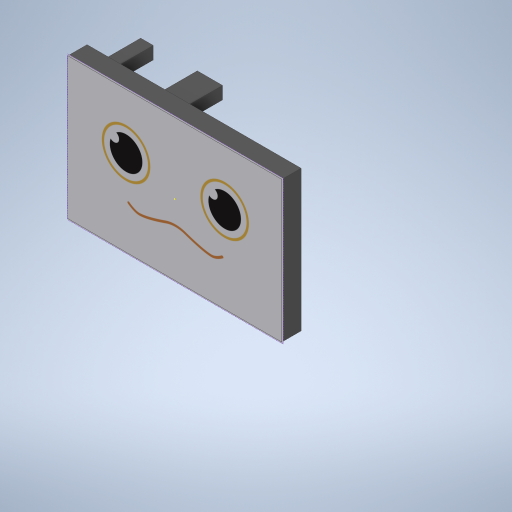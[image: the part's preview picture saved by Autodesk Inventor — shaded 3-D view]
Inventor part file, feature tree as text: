
AUTODESK INVENTOR PART (.ipt)
format: ipt  version: 2023 (Build 270158000, 158)  size: 477,696 bytes
history: native  units: mm
features: extrude x6, sketch x6, projected_geometry x2, fillet x1, other x1
ambient origin geometry x8: Origin, YZ Plane, XZ Plane, XY Plane, X Axis, Y Axis, Z Axis, Center Point
bodies: Body1 (feature_tree)
feature tree (16):
  extrude  "돌출2"  Depth=85.0mm
  extrude  "돌출3"  Depth=56.0mm
  sketch  "스케치5"
  extrude  "돌출4"  Depth=7.65mm TaperAngle=0.0deg
  fillet  "모깎기1"  Radius=5.0mm
  extrude  "돌출5"  Depth=5.0mm
  extrude  "돌출6"  Depth=0.6mm
  extrude  "돌출7"  Depth=0.6mm
  sketch  "스케치9"
  sketch  "스케치2"
  sketch  "스케치4"
  sketch  "스케치6"
  projected_geometry  "투영된 루프1"
  sketch  "스케치7"
  projected_geometry  "투영된 루프2"
  other  "이미지1"
